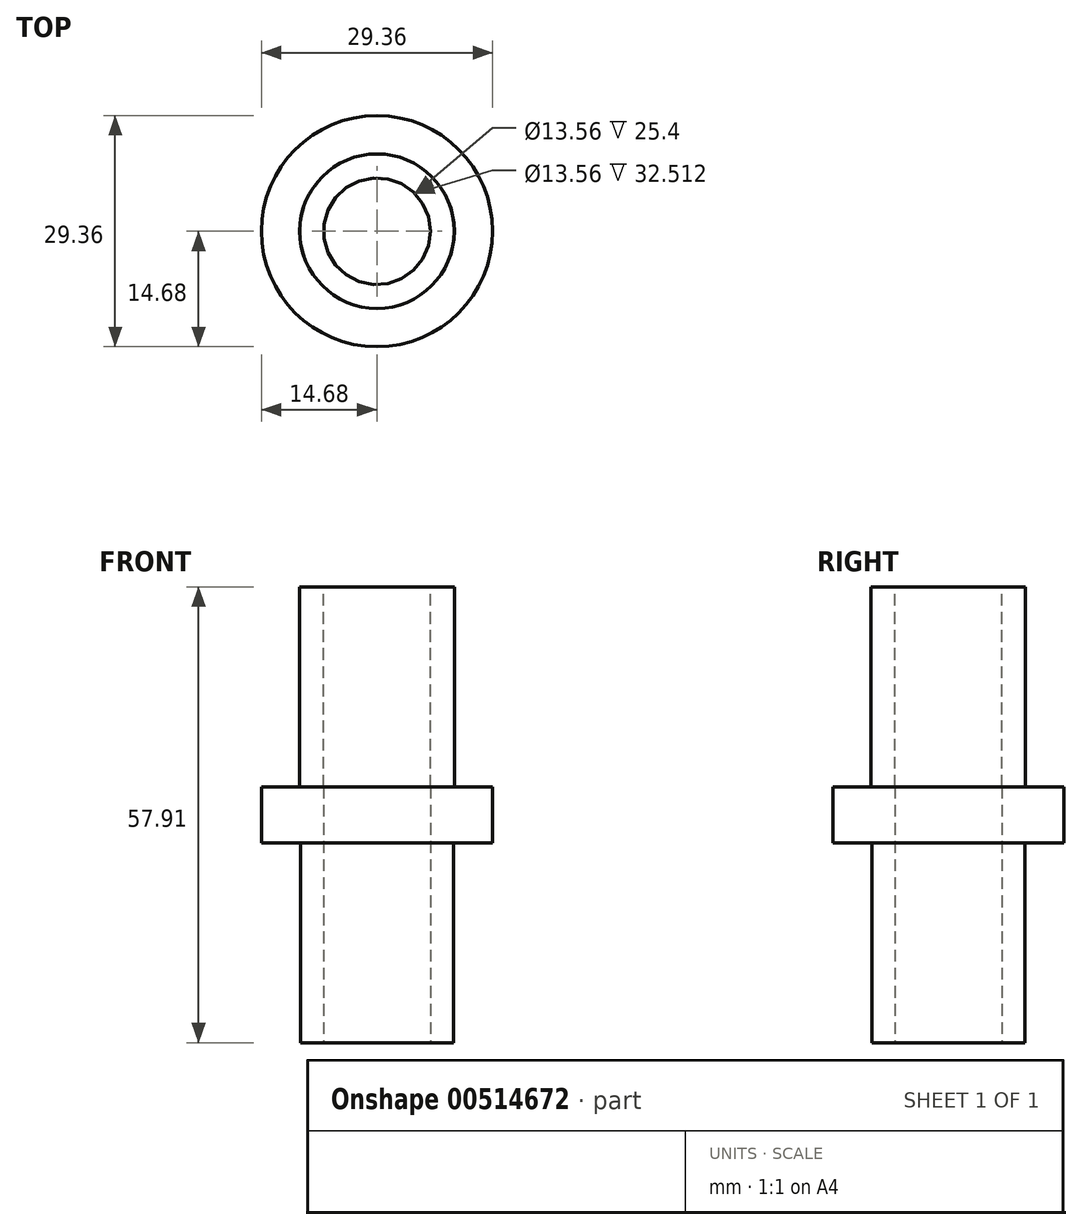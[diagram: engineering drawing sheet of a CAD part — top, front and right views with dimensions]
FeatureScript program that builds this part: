
annotation { "Feature Type Name" : "Feature", "Feature Type Description" : "" }
export const myFeature = defineFeature(function(context is Context, id is Id, definition is map)
    precondition{}
    {
        {
            var Q0;
            Q0=qCreatedBy(makeId("Top.planeOp"),FACE);
            var sketch = newSketch(context, id + "F0", { "sketchPlane" : qUnion([Q0])});
            skCircle(sketch, "E0", {"center": v(0, 0) * mm, "radius": 9.82 * mm});
            skSolve(sketch);
        }
        {
            var Q0;
            Q0=makeQuery(id+"F0.imprint","IMPRINT",FACE,{"disambiguationData":[TD([[makeQuery(id+"F0.imprint","IMPRINT",EDGE,{"derivedFrom":sQuery(id+"F0.wireOp",EDGE,"E0")}),1.0]])]});
            extrude(context, id + "F1", {"entities" : qUnion([Q0]), "depth" : 25.4 * mm, "offsetDistance" : 25.4 * mm});
        }
        {
            var Q0;
            Q0=makeQuery(id+"F1.opExtrude","CAP_FACE",FACE,{"disambiguationData":[OSD([sQuery(id+"F0.wireOp",EDGE,"E0")])],"isStart":false});
            var sketch = newSketch(context, id + "F2", { "sketchPlane" : qUnion([Q0])});
            skSolve(sketch);
        }
        {
            var Q0;
            Q0=makeQuery(id+"F2.imprint","IMPRINT",FACE,{"disambiguationData":[TD([[makeQuery(id+"F2.imprint","IMPRINT",EDGE,{"derivedFrom":makeQuery(id+"F1.opExtrude","CAP_EDGE",EDGE,{"disambiguationData":[OSD([sQuery(id+"F0.wireOp",EDGE,"E0")])],"isStart":false})}),1.0]])]});
            var sketch = newSketch(context, id + "F3", { "sketchPlane" : qUnion([Q0])});
            skCircle(sketch, "E1", {"center": v(0, 0) * mm, "radius": 6.78 * mm});
            skSolve(sketch);
        }
        {
            var Q0;
            Q0 = qSketchRegion(id + "F3", true);
            extrude(context, id + "F4", {"entities" : qUnion([Q0]), "operationType" : NewBodyOperationType.REMOVE, "oppositeDirection" : true, "depth" : 25.4 * mm, "offsetDistance" : 25.4 * mm});
        }
        {
            var Q0;
            Q0=qCreatedBy(makeId("Top.planeOp"),FACE);
            var sketch = newSketch(context, id + "F5", { "sketchPlane" : qUnion([Q0])});
            skCircle(sketch, "E2", {"center": v(0, 0) * mm, "radius": 14.68 * mm});
            skSolve(sketch);
        }
        {
            var Q0;
            Q0 = qSketchRegion(id + "F5", true);
            extrude(context, id + "F6", {"entities" : qUnion([Q0]), "operationType" : NewBodyOperationType.ADD, "oppositeDirection" : true, "depth" : 7.11 * mm, "offsetDistance" : 25.4 * mm});
        }
        {
            var Q0;
            Q0=makeQuery(id+"F6.opExtrude","CAP_FACE",FACE,{"disambiguationData":[OSD([sQuery(id+"F5.wireOp",EDGE,"E2")])],"isStart":false});
            var sketch = newSketch(context, id + "F7", { "sketchPlane" : qUnion([Q0])});
            skCircle(sketch, "E3", {"center": v(0, 0) * mm, "radius": 9.73 * mm});
            skSolve(sketch);
        }
        {
            var Q0;
            Q0 = qSketchRegion(id + "F7", true);
            extrude(context, id + "F8", {"entities" : qUnion([Q0]), "operationType" : NewBodyOperationType.ADD, "depth" : 25.4 * mm, "offsetDistance" : 25.4 * mm});
        }
        {
            var Q0;
            Q0=makeQuery(id+"F8.opExtrude","CAP_FACE",FACE,{"disambiguationData":[OSD([sQuery(id+"F7.wireOp",EDGE,"E3")])],"isStart":false});
            var sketch = newSketch(context, id + "F9", { "sketchPlane" : qUnion([Q0])});
            skCircle(sketch, "E4", {"center": v(0, 0) * mm, "radius": 6.68 * mm});
            skSolve(sketch);
        }
        {
            var Q0;
            Q0=makeQuery(id+"F9.imprint","IMPRINT",FACE,{"disambiguationData":[TD([[makeQuery(id+"F9.imprint","IMPRINT",EDGE,{"derivedFrom":sQuery(id+"F9.wireOp",EDGE,"E4")}),1.0]])]});
            extrude(context, id + "F10", {"entities" : qUnion([Q0]), "operationType" : NewBodyOperationType.ADD, "oppositeDirection" : true, "depth" : 92.46 * mm, "offsetDistance" : 25.4 * mm});
        }
        {
            var Q0;
            Q0=sQuery(id+"F9.wireOp",VERTEX,"E4.center");
            var Q1;
            Q1=makeQuery(id+"F1.opExtrude","SWEPT_BODY",BODY,{"disambiguationData":[OSD([sQuery(id+"F0.wireOp",EDGE,"E0")])]});
            hole(context, id + "F11", {"style" : HoleStyle.SIMPLE, "endStyle" : HoleEndStyle.THROUGH, "holeDiameter" : 13.56 * mm, "isTappedThrough" : true, "tappedDepth" : 12.7 * mm, "tapClearance" : 3, "locations" : qUnion([Q0]), "scope" : qUnion([Q1])});
        }
    });
